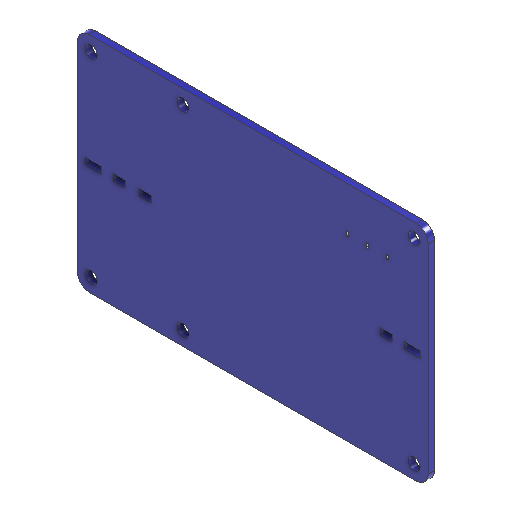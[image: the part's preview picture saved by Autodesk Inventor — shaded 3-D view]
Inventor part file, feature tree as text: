
AUTODESK INVENTOR PART (.ipt)
format: ipt  version: 2025.2 (Build 292293000, 293)  size: 186,880 bytes
history: native  units: mm
features: sketch x4, extrude x3, hole x1
ambient origin geometry x8: Origin, YZ Plane, XZ Plane, XY Plane, X Axis, Y Axis, Z Axis, Center Point
bodies: Solid1 (feature_tree)
feature tree (8):
  extrude  "Extrusion1"  Depth=56.0mm
  extrude  "Extrusion2"  Depth=1.6mm TaperAngle=0.0deg
  hole  "Hole1"  [1 undecoded]
  extrude  "Extrusion3"  Depth=3.0mm
  sketch  "Sketch1"  dims[d0=88.0mm d1=56.0mm]
  sketch  "Sketch2"  dims[d2=3.0mm d3=1.6mm d4=0.0mm]
  sketch  "Sketch3"  dims[d5=2.0mm d6=4.0mm]
  sketch  "Sketch4"  dims[d7=3.0mm d8=3.0mm d9=3.5mm d10=2.0mm d11=4.0mm d12=3.0mm d13=3.0mm d14=1.6mm d15=1.6mm d16=0.0mm d17=3.0mm d18=6.0mm d19=4.0mm d20=2.0mm d21=90.0deg d22=1.0mm d23=20.594885mm d24=58.0mm d25=23.0mm d26=49.0mm d27=3.5mm d28=0.5mm d29=5.0mm d30=5.0mm d31=11.5mm d32=1.0mm d33=10.0mm d34=0.0mm d35=0.0mm]
note: 1 required parameter value undecoded (feature->parameter linkage not recoverable at this tier; creation-order binding heuristic only, values carry confidence <= 0.55)
